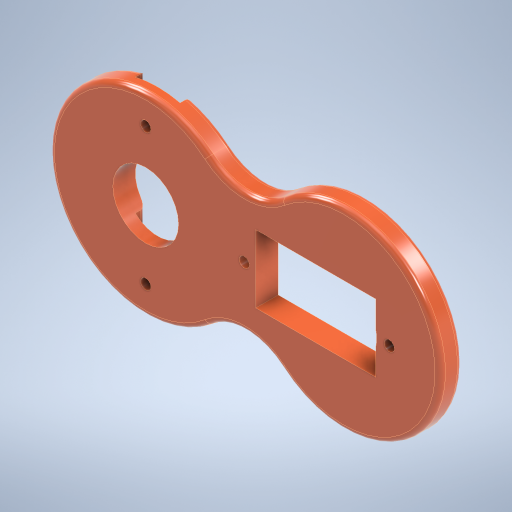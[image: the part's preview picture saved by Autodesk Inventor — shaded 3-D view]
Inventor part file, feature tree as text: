
AUTODESK INVENTOR PART (.ipt)
format: ipt  version: 2023.2 (Build 272271000, 271)  size: 365,568 bytes
history: native  units: mm
features: sketch x5, extrude x3, hole x2, fillet x1
ambient origin geometry x8: Origin, YZ Plane, XZ Plane, XY Plane, X Axis, Y Axis, Z Axis, Center Point
bodies: Solid1 (feature_tree)
feature tree (11):
  extrude  "Extrusion1"  Depth=4.3mm TaperAngle=0.0deg
  hole  "Hole1"  [1 undecoded]
  extrude  "Extrusion2"  Depth=2.0mm
  extrude  "Extrusion3"  Depth=2.0mm
  fillet  "Fillet1"  Radius=23.0mm
  hole  "Hole2"  [1 undecoded]
  sketch  "Sketch2"  dims[d0=37.0mm d5=4.3mm d6=0.0mm]
  sketch  "Sketch3"  dims[d7=27.8mm]
  sketch  "Sketch4"  dims[d8=2.0mm d9=6.0mm d10=4.0mm d11=2.0mm d12=90.0deg d13=7.0mm d14=0.0mm d16=8.7mm]
  sketch  "Sketch5"  dims[d17=2.0mm d18=0.0mm d19=12.6mm]
  sketch  "Sketch7"  dims[d20=37.0mm d21=13.0mm d22=23.0mm d23=2.6mm d24=4.3mm d25=0.0mm d26=38.0mm d27=1.0mm d28=26.2mm d29=2.0mm d30=6.0mm d31=4.0mm d32=2.0mm d33=90.0deg d34=7.0mm d35=0.0mm]
note: 2 required parameter values undecoded (feature->parameter linkage not recoverable at this tier; creation-order binding heuristic only, values carry confidence <= 0.55)
